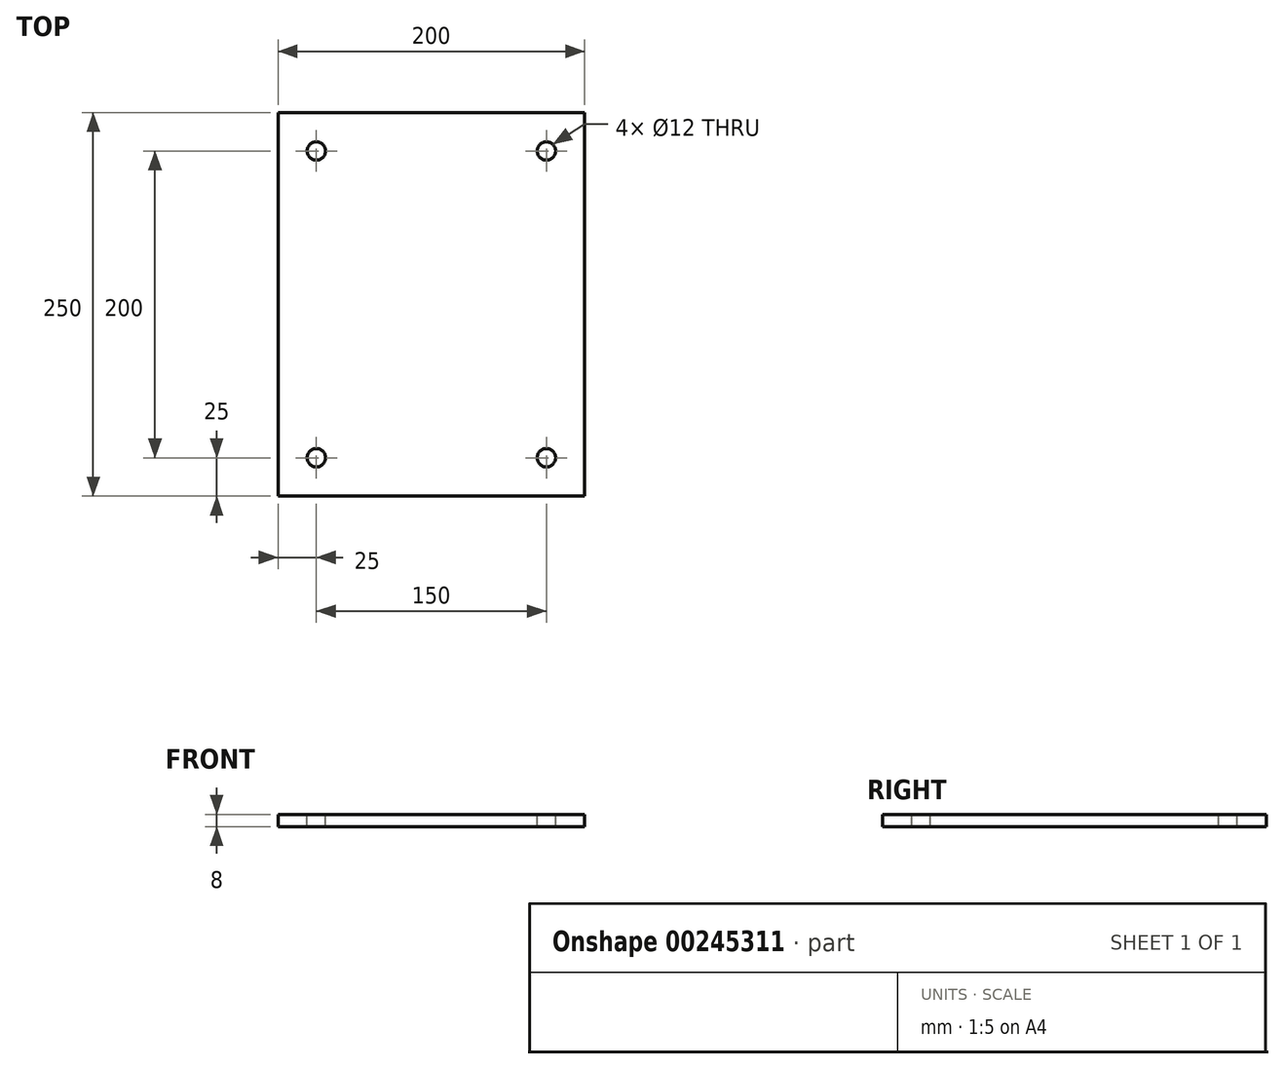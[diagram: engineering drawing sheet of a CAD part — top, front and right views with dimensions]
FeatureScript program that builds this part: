
annotation { "Feature Type Name" : "Feature", "Feature Type Description" : "" }
export const myFeature = defineFeature(function(context is Context, id is Id, definition is map)
    precondition{}
    {
        {
            var Q0;
            Q0=qCreatedBy(makeId("Top.planeOp"),FACE);
            var sketch = newSketch(context, id + "F0", { "sketchPlane" : qUnion([Q0])});
            skLineSegment(sketch, "E0.bottom", {"start": v(0, 0) * mm, "end": v(200, 0) * mm});
            skLineSegment(sketch, "E0.top", {"start": v(0, 250) * mm, "end": v(200, 250) * mm});
            skLineSegment(sketch, "E0.left", {"start": v(0, 0) * mm, "end": v(0, 250) * mm});
            skLineSegment(sketch, "E0.right", {"start": v(200, 0) * mm, "end": v(200, 250) * mm});
            skSolve(sketch);
        }
        {
            var Q0;
            Q0 = qSketchRegion(id + "F0", true);
            extrude(context, id + "F1", {"entities" : qUnion([Q0]), "depth" : 8 * mm, "offsetDistance" : 25 * mm});
        }
        {
            var Q0;
            Q0=makeQuery(id+"F1.opExtrude","CAP_FACE",FACE,{"disambiguationData":[OSD([sQuery(id+"F0.wireOp",EDGE,"E0.bottom"),sQuery(id+"F0.wireOp",EDGE,"E0.top"),sQuery(id+"F0.wireOp",EDGE,"E0.left"),sQuery(id+"F0.wireOp",EDGE,"E0.right")])],"isStart":false});
            var sketch = newSketch(context, id + "F2", { "sketchPlane" : qUnion([Q0])});
            skPoint(sketch, "E1", {"position": v(25, 225) * mm});
            skPoint(sketch, "E2", {"position": v(175, 225) * mm});
            skPoint(sketch, "E3", {"position": v(175, 25) * mm});
            skPoint(sketch, "E4", {"position": v(25, 25) * mm});
            skSolve(sketch);
        }
        {
            var Q0;
            Q0=sQuery(id+"F2.wireOp",VERTEX,"E1");
            var Q1;
            Q1=sQuery(id+"F2.wireOp",VERTEX,"E4");
            var Q2;
            Q2=sQuery(id+"F2.wireOp",VERTEX,"E2");
            var Q3;
            Q3=sQuery(id+"F2.wireOp",VERTEX,"E2");
            var Q4;
            Q4=sQuery(id+"F2.wireOp",VERTEX,"E3");
            var Q5;
            Q5=makeQuery(id+"F1.opExtrude","SWEPT_BODY",BODY,{"disambiguationData":[OSD([sQuery(id+"F0.wireOp",EDGE,"E0.bottom"),sQuery(id+"F0.wireOp",EDGE,"E0.top"),sQuery(id+"F0.wireOp",EDGE,"E0.left"),sQuery(id+"F0.wireOp",EDGE,"E0.right")])]});
            hole(context, id + "F3", {"style" : HoleStyle.SIMPLE, "endStyle" : HoleEndStyle.THROUGH, "holeDiameter" : 12 * mm, "majorDiameter" : 5 * mm, "isTappedThrough" : true, "tappedDepth" : 28 * mm, "tapClearance" : 3, "locations" : qUnion([Q0, Q1, Q2, Q3, Q4]), "scope" : qUnion([Q5])});
        }
    });
